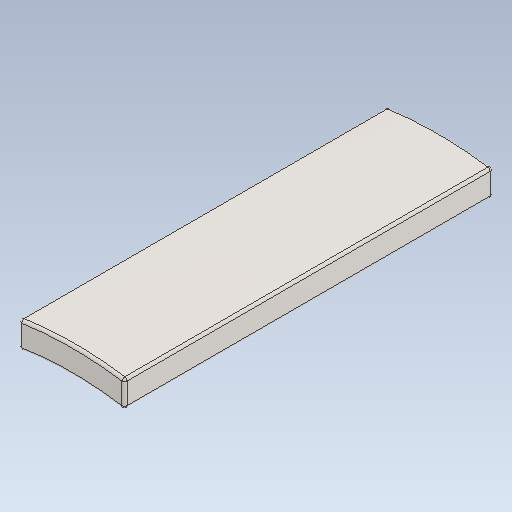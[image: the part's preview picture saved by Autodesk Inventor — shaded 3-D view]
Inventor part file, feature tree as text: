
AUTODESK INVENTOR PART (.ipt)
format: ipt  version: 2021 (Build 250183000, 183)  size: 107,520 bytes
history: mixed  units: mm
features: other x1, fillet x1, imported_body x1
ambient origin geometry x8: Origin, YZ Plane, XZ Plane, XY Plane, X Axis, Y Axis, Z Axis, Center Point
bodies: Body1 (imported_parasolid)
feature tree (3):
  other  "솔리드1"
  fillet  "Fillet1"  [1 undecoded]
  imported_body  NMx_Import_Brep_tag  [imported B-rep: ~26 faces, bbox_mm=[4.0, 1.007084, 14.0]]
note: 1 required parameter value undecoded (feature->parameter linkage not recoverable at this tier; creation-order binding heuristic only, values carry confidence <= 0.55)
